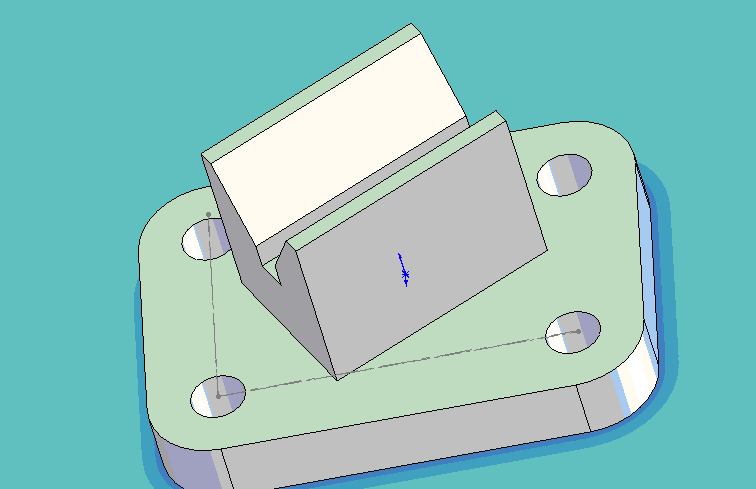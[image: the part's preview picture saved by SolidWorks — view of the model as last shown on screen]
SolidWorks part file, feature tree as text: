
SOLIDWORKS PART (.sldprt)
format: sldprt  version: not decoded by parser v0  size: 131,072 bytes
history: native  units: mm
features: sketch x5, plane x3, extrude x2, cut_extrude x2, material x1, pattern_linear x1, fillet x1 (+10 scaffold rows collapsed)
feature tree (25):
  scaffold x10  (default folders/planes/origin — collapsed)
  material  "Material <not specified>"
  plane  "Frontal"
  plane  "Horizontal"
  plane  "Profile"
  sketch  "Sketch1"  dims[D1=88.9mm D2=63.5mm]
  extrude  "Extrude1"  Depth=12.192mm
  sketch  "Sketch2"  dims[D1=12.7mm D2=12.7mm]
  cut_extrude  "Cut-Extrude1"  [1 undecoded]
  sketch  "Sketch3"
  pattern_linear  "LPattern1"  Count1=2 Count2=2 Spacing1=63.5mm Spacing2=38.1mm
  fillet  "Fillet1"  Radius=12.7mm
  sketch  "Sketch4"  dims[c1.D1=~34.300437mm c2.D1=120.0deg c3.D1=31.75mm c3.D2=44.45mm]
  extrude  "Extrude2"  Depth=33.782mm
  sketch  "Sketch5"  dims[c1.D1=~10.70578mm c2.D1=90.0deg c3.D1=6.35mm c3.D2=3.302mm c3.D3=3.302mm c3.D4=19.05mm c3.D5=5.08mm]
  cut_extrude  "Cut-Extrude3"  [1 undecoded]
decode coverage: 8 of 11 modeling features carry decoded parameters
note: ~ marks probable driven/reference dimensions
note: 2 parameter values undecoded
note: suppression state not decoded; provenance and decode notes live in map.json
